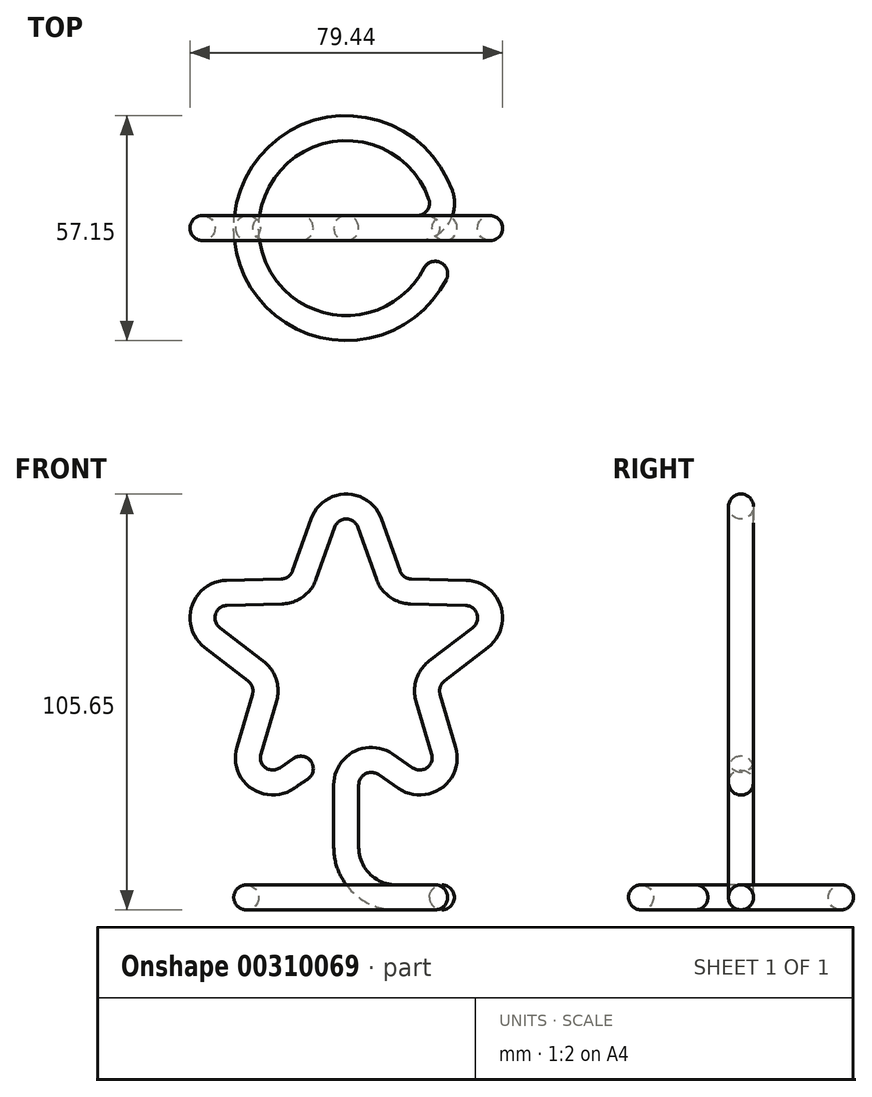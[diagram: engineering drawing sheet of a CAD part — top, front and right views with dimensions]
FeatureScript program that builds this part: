
annotation { "Feature Type Name" : "Feature", "Feature Type Description" : "" }
export const myFeature = defineFeature(function(context is Context, id is Id, definition is map)
    precondition{}
    {
        {
            var Q0;
            Q0=qCreatedBy(makeId("Front.planeOp"),FACE);
            var sketch = newSketch(context, id + "F0", { "sketchPlane" : qUnion([Q0])});
            skLineSegment(sketch, "E0", {"start": v(0, 12.7) * mm, "end": v(0, 28.58) * mm});
            skCircle(sketch, "E1.cCircle", {"center": v(0, 61.2) * mm, "radius": 25.4 * mm, "construction": true});
            skLineSegment(sketch, "E1.0", {"start": v(14.93, 40.65) * mm, "end": v(-14.93, 40.65) * mm, "construction": true});
            skLineSegment(sketch, "E1.1", {"start": v(-14.93, 40.65) * mm, "end": v(-24.16, 69.05) * mm, "construction": true});
            skLineSegment(sketch, "E1.2", {"start": v(-24.16, 69.05) * mm, "end": v(0, 86.6) * mm, "construction": true});
            skLineSegment(sketch, "E1.3", {"start": v(0, 86.6) * mm, "end": v(24.16, 69.05) * mm, "construction": true});
            skLineSegment(sketch, "E1.4", {"start": v(24.16, 69.05) * mm, "end": v(14.93, 40.65) * mm, "construction": true});
            skLineSegment(sketch, "E2", {"start": v(0, 61.2) * mm, "end": v(-48.31, 76.9) * mm, "construction": true});
            skLineSegment(sketch, "E3", {"start": v(0, 61.2) * mm, "end": v(0, 112) * mm, "construction": true});
            skLineSegment(sketch, "E4", {"start": v(0, 61.2) * mm, "end": v(48.31, 76.9) * mm, "construction": true});
            skLineSegment(sketch, "E5", {"start": v(0, 61.2) * mm, "end": v(29.86, 20.1) * mm, "construction": true});
            skLineSegment(sketch, "E6", {"start": v(0, 61.2) * mm, "end": v(-29.86, 20.1) * mm, "construction": true});
            skLineSegment(sketch, "E7", {"start": v(9.95, 33.8) * mm, "end": v(15.06, 30.3) * mm});
            skLineSegment(sketch, "E8", {"start": v(20.79, 50.66) * mm, "end": v(24.75, 37.33) * mm});
            skLineSegment(sketch, "E9", {"start": v(23.01, 57.51) * mm, "end": v(34.05, 65.97) * mm});
            skLineSegment(sketch, "E10", {"start": v(30.35, 77.36) * mm, "end": v(16.45, 77.72) * mm});
            skLineSegment(sketch, "E11", {"start": v(10.62, 81.95) * mm, "end": v(5.99, 95.06) * mm});
            skLineSegment(sketch, "E12", {"start": v(-10.62, 81.95) * mm, "end": v(-5.99, 95.06) * mm});
            skLineSegment(sketch, "E13", {"start": v(-16.45, 77.72) * mm, "end": v(-30.35, 77.36) * mm});
            skLineSegment(sketch, "E14", {"start": v(-20.79, 50.66) * mm, "end": v(-24.75, 37.33) * mm});
            skLineSegment(sketch, "E15", {"start": v(-34.05, 65.97) * mm, "end": v(-23.01, 57.51) * mm});
            skLineSegment(sketch, "E16", {"start": v(-15.06, 30.3) * mm, "end": v(-8.94, 34.5) * mm});
            skLineSegment(sketch, "E17", {"start": v(0, 40.65) * mm, "end": v(-15.06, 30.3) * mm, "construction": true});
            skArc(sketch, "E18", {"start": v(-30.35, 77.36) * mm, "mid": v(-36.23, 72.97) * mm, "end": v(-34.05, 65.97) * mm});
            skArc(sketch, "E19", {"start": v(5.99, 95.06) * mm, "mid": v(0, 99.3) * mm, "end": v(-5.99, 95.06) * mm});
            skArc(sketch, "E20", {"start": v(34.05, 65.97) * mm, "mid": v(36.23, 72.97) * mm, "end": v(30.35, 77.36) * mm});
            skArc(sketch, "E21", {"start": v(15.06, 30.3) * mm, "mid": v(22.4, 30.38) * mm, "end": v(24.75, 37.33) * mm});
            skArc(sketch, "E22", {"start": v(-24.75, 37.33) * mm, "mid": v(-22.4, 30.38) * mm, "end": v(-15.06, 30.3) * mm});
            skArc(sketch, "E23", {"start": v(9.95, 33.8) * mm, "mid": v(3.4, 34.2) * mm, "end": v(0, 28.58) * mm});
            skArc(sketch, "E24", {"start": v(0, 12.7) * mm, "mid": v(3.72, 3.72) * mm, "end": v(12.7, 0) * mm});
            skPoint(sketch, "E25.orphan", {"position": v(0, 0) * mm});
            skArc(sketch, "E26", {"start": v(-16.45, 77.72) * mm, "mid": v(-12.88, 78.93) * mm, "end": v(-10.62, 81.95) * mm});
            skArc(sketch, "E27", {"start": v(-20.79, 50.66) * mm, "mid": v(-20.84, 54.43) * mm, "end": v(-23.01, 57.51) * mm});
            skArc(sketch, "E28", {"start": v(23.01, 57.51) * mm, "mid": v(20.84, 54.43) * mm, "end": v(20.79, 50.66) * mm});
            skArc(sketch, "E29", {"start": v(10.62, 81.95) * mm, "mid": v(12.88, 78.93) * mm, "end": v(16.45, 77.72) * mm});
            skPoint(sketch, "E30.orphan", {"position": v(-12.08, 77.83) * mm});
            skPoint(sketch, "E31.orphan", {"position": v(12.08, 77.83) * mm});
            skPoint(sketch, "E32.orphan", {"position": v(19.54, 54.85) * mm});
            skPoint(sketch, "E33.orphan", {"position": v(-19.54, 54.85) * mm});
            skLineSegment(sketch, "E34", {"start": v(0, 0) * mm, "end": v(12.7, 0) * mm, "construction": true});
            skSolve(sketch);
        }
        {
            var Q0;
            Q0=qCreatedBy(makeId("Top.planeOp"),FACE);
            var sketch = newSketch(context, id + "F1", { "sketchPlane" : qUnion([Q0])});
            skArc(sketch, "E35", {"start": v(23.95, 8.47) * mm, "mid": v(-25.4, 0.12) * mm, "end": v(23.87, -8.69) * mm});
            skLineSegment(sketch, "E36", {"start": v(0, 0) * mm, "end": v(23.87, -8.69) * mm, "construction": true});
            skArc(sketch, "E37", {"start": v(17.96, 0) * mm, "mid": v(23.15, 2.68) * mm, "end": v(23.95, 8.47) * mm});
            skLineSegment(sketch, "E38", {"start": v(0, 0) * mm, "end": v(28.57, 0) * mm, "construction": true});
            skLineSegment(sketch, "E39", {"start": v(17.96, 0) * mm, "end": v(12.7, 0) * mm});
            skSolve(sketch);
        }
        {
            var Q0;
            Q0=sQuery(id+"F1.wireOp",EDGE,"E36");
            cPlane(context, id + "F2", {"entities" : qUnion([Q0]), "cplaneType" : CPlaneType.LINE_ANGLE, "offset" : 25.4 * mm, "angle" : 0 * degree, "width" : 152.4 * mm, "height" : 152.4 * mm});
        }
        {
            var Q0;
            Q0=qCreatedBy(id+"F2.planeOp",FACE);
            var sketch = newSketch(context, id + "F3", { "sketchPlane" : qUnion([Q0])});
            skCircle(sketch, "E40", {"center": v(-25.4, 0) * mm, "radius": 3.18 * mm});
            skSolve(sketch);
        }
        {
            var Q0;
            Q0=makeQuery(id+"F3.imprint","IMPRINT",FACE,{"disambiguationData":[TD([[makeQuery(id+"F3.imprint","IMPRINT",EDGE,{"derivedFrom":sQuery(id+"F3.wireOp",EDGE,"E40")}),1.0]])]});
            var Q1;
            Q1=sQuery(id+"F1.wireOp",EDGE,"E35");
            var Q2;
            Q2=sQuery(id+"F1.wireOp",EDGE,"E37");
            var Q3;
            Q3=sQuery(id+"F1.wireOp",EDGE,"E39");
            var Q4;
            Q4=sQuery(id+"F0.wireOp",EDGE,"E24");
            var Q5;
            Q5=sQuery(id+"F0.wireOp",EDGE,"E0");
            var Q6;
            Q6=sQuery(id+"F0.wireOp",EDGE,"E23");
            var Q7;
            Q7=sQuery(id+"F0.wireOp",EDGE,"E7");
            var Q8;
            Q8=sQuery(id+"F0.wireOp",EDGE,"E21");
            var Q9;
            Q9=sQuery(id+"F0.wireOp",EDGE,"E8");
            var Q10;
            Q10=sQuery(id+"F0.wireOp",EDGE,"E28");
            var Q11;
            Q11=sQuery(id+"F0.wireOp",EDGE,"E9");
            var Q12;
            Q12=sQuery(id+"F0.wireOp",EDGE,"E20");
            var Q13;
            Q13=sQuery(id+"F0.wireOp",EDGE,"E10");
            var Q14;
            Q14=sQuery(id+"F0.wireOp",EDGE,"E29");
            var Q15;
            Q15=sQuery(id+"F0.wireOp",EDGE,"E11");
            var Q16;
            Q16=sQuery(id+"F0.wireOp",EDGE,"E19");
            var Q17;
            Q17=sQuery(id+"F0.wireOp",EDGE,"E12");
            var Q18;
            Q18=sQuery(id+"F0.wireOp",EDGE,"E26");
            var Q19;
            Q19=sQuery(id+"F0.wireOp",EDGE,"E13");
            var Q20;
            Q20=sQuery(id+"F0.wireOp",EDGE,"E18");
            var Q21;
            Q21=sQuery(id+"F0.wireOp",EDGE,"E15");
            var Q22;
            Q22=sQuery(id+"F0.wireOp",EDGE,"E27");
            var Q23;
            Q23=sQuery(id+"F0.wireOp",EDGE,"E14");
            var Q24;
            Q24=sQuery(id+"F0.wireOp",EDGE,"E22");
            var Q25;
            Q25=sQuery(id+"F0.wireOp",EDGE,"E16");
            sweep(context, id + "F4", {"profiles" : qUnion([Q0]), "path" : qUnion([Q1, Q2, Q3, Q4, Q5, Q6, Q7, Q8, Q9, Q10, Q11, Q12, Q13, Q14, Q15, Q16, Q17, Q18, Q19, Q20, Q21, Q22, Q23, Q24, Q25])});
        }
        {
            var Q0;
            Q0=makeQuery(id+"F4.opSweep","CAP_EDGE",EDGE,{"disambiguationData":[OSD([sQuery(id+"F1.wireOp",VERTEX,"E35.end"),sQuery(id+"F3.wireOp",EDGE,"E40")])],"isStart":true});
            var Q1;
            Q1=makeQuery(id+"F4.opSweep","CAP_EDGE",EDGE,{"disambiguationData":[OSD([sQuery(id+"F0.wireOp",VERTEX,"E16.end"),sQuery(id+"F3.wireOp",EDGE,"E40")])],"isStart":false});
            fillet(context, id + "F5", {"entities" : qUnion([Q0, Q1]), "radius" : 3.17 * mm, "tangentPropagation" : true, "allowEdgeOverflow" : false});
        }
    });
